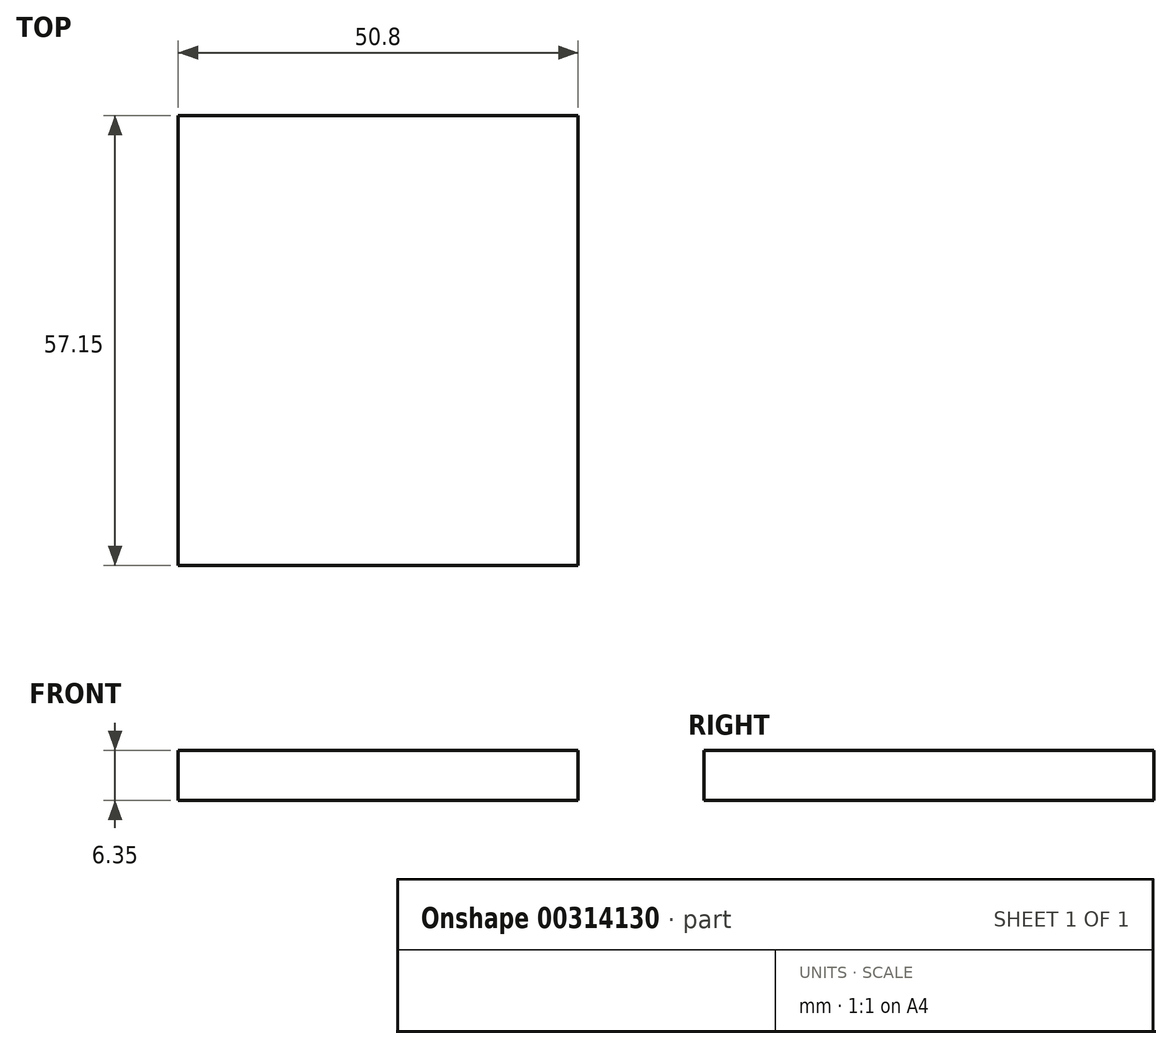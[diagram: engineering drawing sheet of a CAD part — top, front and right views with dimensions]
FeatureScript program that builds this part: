
annotation { "Feature Type Name" : "Feature", "Feature Type Description" : "" }
export const myFeature = defineFeature(function(context is Context, id is Id, definition is map)
    precondition{}
    {
        {
            var Q0;
            Q0=qCreatedBy(makeId("Top.planeOp"),FACE);
            var sketch = newSketch(context, id + "F0", { "sketchPlane" : qUnion([Q0])});
            skLineSegment(sketch, "E0.bottom", {"start": v(0, 0) * mm, "end": v(50.8, 0) * mm});
            skLineSegment(sketch, "E0.top", {"start": v(0, 57.15) * mm, "end": v(50.8, 57.15) * mm});
            skLineSegment(sketch, "E0.left", {"start": v(0, 0) * mm, "end": v(0, 57.15) * mm});
            skLineSegment(sketch, "E0.right", {"start": v(50.8, 0) * mm, "end": v(50.8, 57.15) * mm});
            skSolve(sketch);
        }
        {
            var Q0;
            Q0=makeQuery(id+"F0.imprint","IMPRINT",FACE,{"disambiguationData":[TD([[makeQuery(id+"F0.imprint","IMPRINT",EDGE,{"derivedFrom":sQuery(id+"F0.wireOp",EDGE,"E0.bottom")}),1.0]])]});
            extrude(context, id + "F1", {"entities" : qUnion([Q0]), "depth" : 6.35 * mm});
        }
    });
